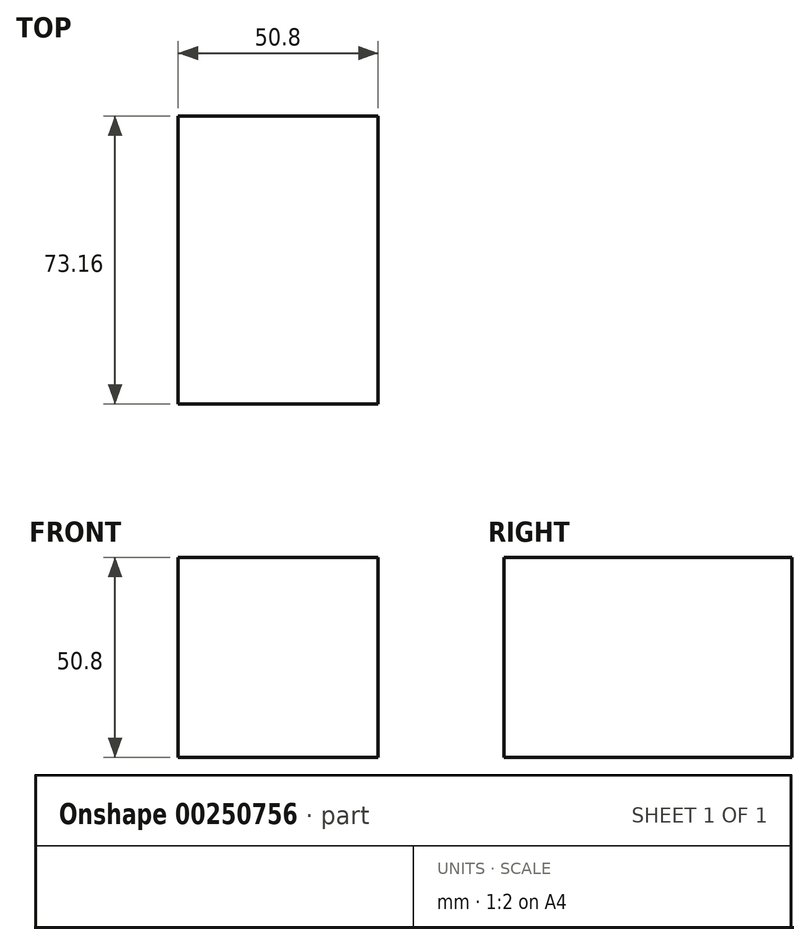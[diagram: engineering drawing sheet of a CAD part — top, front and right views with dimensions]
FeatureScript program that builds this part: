
annotation { "Feature Type Name" : "Feature", "Feature Type Description" : "" }
export const myFeature = defineFeature(function(context is Context, id is Id, definition is map)
    precondition{}
    {
        {
            var Q0;
            Q0=qCreatedBy(makeId("Front.planeOp"),FACE);
            var sketch = newSketch(context, id + "F0", { "sketchPlane" : qUnion([Q0])});
            skLineSegment(sketch, "E0.bottom", {"start": v(25.4, -25.4) * mm, "end": v(-25.4, -25.4) * mm});
            skLineSegment(sketch, "E0.top", {"start": v(25.4, 25.4) * mm, "end": v(-25.4, 25.4) * mm});
            skLineSegment(sketch, "E0.left", {"start": v(25.4, -25.4) * mm, "end": v(25.4, 25.4) * mm});
            skLineSegment(sketch, "E0.right", {"start": v(-25.4, -25.4) * mm, "end": v(-25.4, 25.4) * mm});
            skPoint(sketch, "E0.middle", {"position": v(0, 0) * mm});
            skSolve(sketch);
        }
        {
            var Q0;
            Q0=makeQuery(id+"F0.imprint","IMPRINT",FACE,{"disambiguationData":[TD([[makeQuery(id+"F0.imprint","IMPRINT",EDGE,{"derivedFrom":sQuery(id+"F0.wireOp",EDGE,"E0.bottom")}),-1.0]])]});
            extrude(context, id + "F1", {"entities" : qUnion([Q0]), "endBound" : BoundingType.SYMMETRIC, "depth" : 73.15 * mm});
        }
    });
